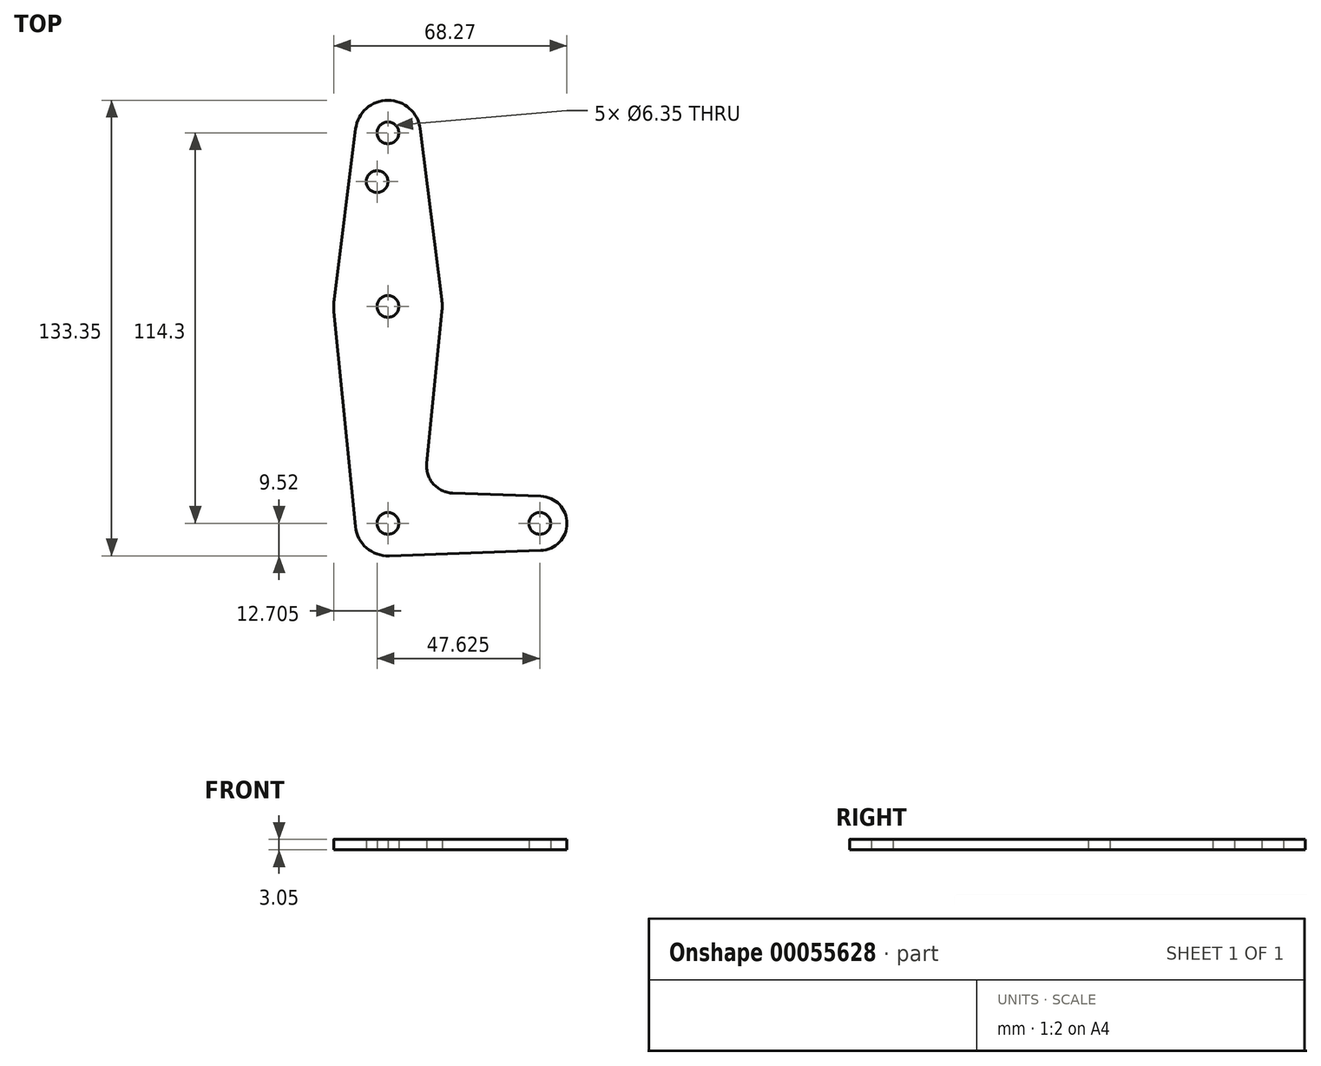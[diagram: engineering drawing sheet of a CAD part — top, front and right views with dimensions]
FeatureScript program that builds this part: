
annotation { "Feature Type Name" : "Feature", "Feature Type Description" : "" }
export const myFeature = defineFeature(function(context is Context, id is Id, definition is map)
    precondition{}
    {
        {
            var Q0;
            Q0=qCreatedBy(makeId("Top.planeOp"),FACE);
            var sketch = newSketch(context, id + "F0", { "sketchPlane" : qUnion([Q0])});
            skCircle(sketch, "E0", {"center": v(0, 0) * mm, "radius": 9.53 * mm});
            skLineSegment(sketch, "E1", {"start": v(0, 0) * mm, "end": v(0, 114.3) * mm, "construction": true});
            skLineSegment(sketch, "E2", {"start": v(0, 0) * mm, "end": v(44.45, 0) * mm, "construction": true});
            skCircle(sketch, "E3", {"center": v(44.45, 0) * mm, "radius": 7.94 * mm});
            skCircle(sketch, "E4", {"center": v(0, 114.3) * mm, "radius": 9.53 * mm});
            skCircle(sketch, "E5", {"center": v(0, 63.5) * mm, "radius": 15.88 * mm});
            skLineSegment(sketch, "E6", {"start": v(-9.45, 115.5) * mm, "end": v(-15.75, 65.48) * mm});
            skLineSegment(sketch, "E7", {"start": v(-15.8, 61.91) * mm, "end": v(-9.48, -0.95) * mm});
            skLineSegment(sketch, "E8", {"start": v(0.34, -9.52) * mm, "end": v(44.73, -7.93) * mm});
            skLineSegment(sketch, "E9", {"start": v(44.73, 7.93) * mm, "end": v(18.97, 8.85) * mm});
            skLineSegment(sketch, "E10", {"start": v(11.34, 17.6) * mm, "end": v(15.8, 61.91) * mm});
            skLineSegment(sketch, "E11", {"start": v(9.45, 115.5) * mm, "end": v(15.75, 65.48) * mm});
            skCircle(sketch, "E12", {"center": v(0, 114.3) * mm, "radius": 3.18 * mm});
            skCircle(sketch, "E13", {"center": v(0, 63.5) * mm, "radius": 3.18 * mm});
            skCircle(sketch, "E14", {"center": v(0, 0) * mm, "radius": 3.18 * mm});
            skCircle(sketch, "E15", {"center": v(44.45, 0) * mm, "radius": 3.18 * mm});
            skCircle(sketch, "E16", {"center": v(-3.18, 100.03) * mm, "radius": 3.18 * mm});
            skArc(sketch, "E17.filletArc", {"start": v(11.34, 17.6) * mm, "mid": v(13.26, 11.57) * mm, "end": v(18.97, 8.85) * mm});
            skSolve(sketch);
        }
        {
            var Q0;
            {var subQ0=sQuery(id+"F0.wireOp",EDGE,"E7");Q0=makeQuery(id+"F0.imprint","IMPRINT",FACE,{"disambiguationData":[TD([[makeQuery(id+"F0.imprint","IMPRINT",EDGE,{"derivedFrom":subQ0}),1.0]])]});}
            var Q1;
            {var subQ1=sQuery(id+"F0.wireOp",EDGE,"E6");Q1=makeQuery(id+"F0.imprint","IMPRINT",FACE,{"disambiguationData":[TD([[makeQuery(id+"F0.imprint","IMPRINT",EDGE,{"derivedFrom":subQ1}),1.0]])]});}
            var Q2;
            Q2=makeQuery(id+"F0.imprint","IMPRINT",FACE,{"disambiguationData":[TD([[makeQuery(id+"F0.imprint","IMPRINT",EDGE,{"derivedFrom":sQuery(id+"F0.wireOp",EDGE,"E12")}),-1.0]])]});
            var Q3;
            Q3=makeQuery(id+"F0.imprint","IMPRINT",FACE,{"disambiguationData":[TD([[makeQuery(id+"F0.imprint","IMPRINT",EDGE,{"derivedFrom":sQuery(id+"F0.wireOp",EDGE,"E13")}),-1.0]])]});
            var Q4;
            Q4=makeQuery(id+"F0.imprint","IMPRINT",FACE,{"disambiguationData":[TD([[makeQuery(id+"F0.imprint","IMPRINT",EDGE,{"derivedFrom":sQuery(id+"F0.wireOp",EDGE,"E14")}),-1.0]])]});
            var Q5;
            Q5=makeQuery(id+"F0.imprint","IMPRINT",FACE,{"disambiguationData":[TD([[makeQuery(id+"F0.imprint","IMPRINT",EDGE,{"derivedFrom":sQuery(id+"F0.wireOp",EDGE,"E15")}),-1.0]])]});
            extrude(context, id + "F1", {"entities" : qUnion([Q0, Q1, Q2, Q3, Q4, Q5]), "depth" : 3.05 * mm});
        }
    });
